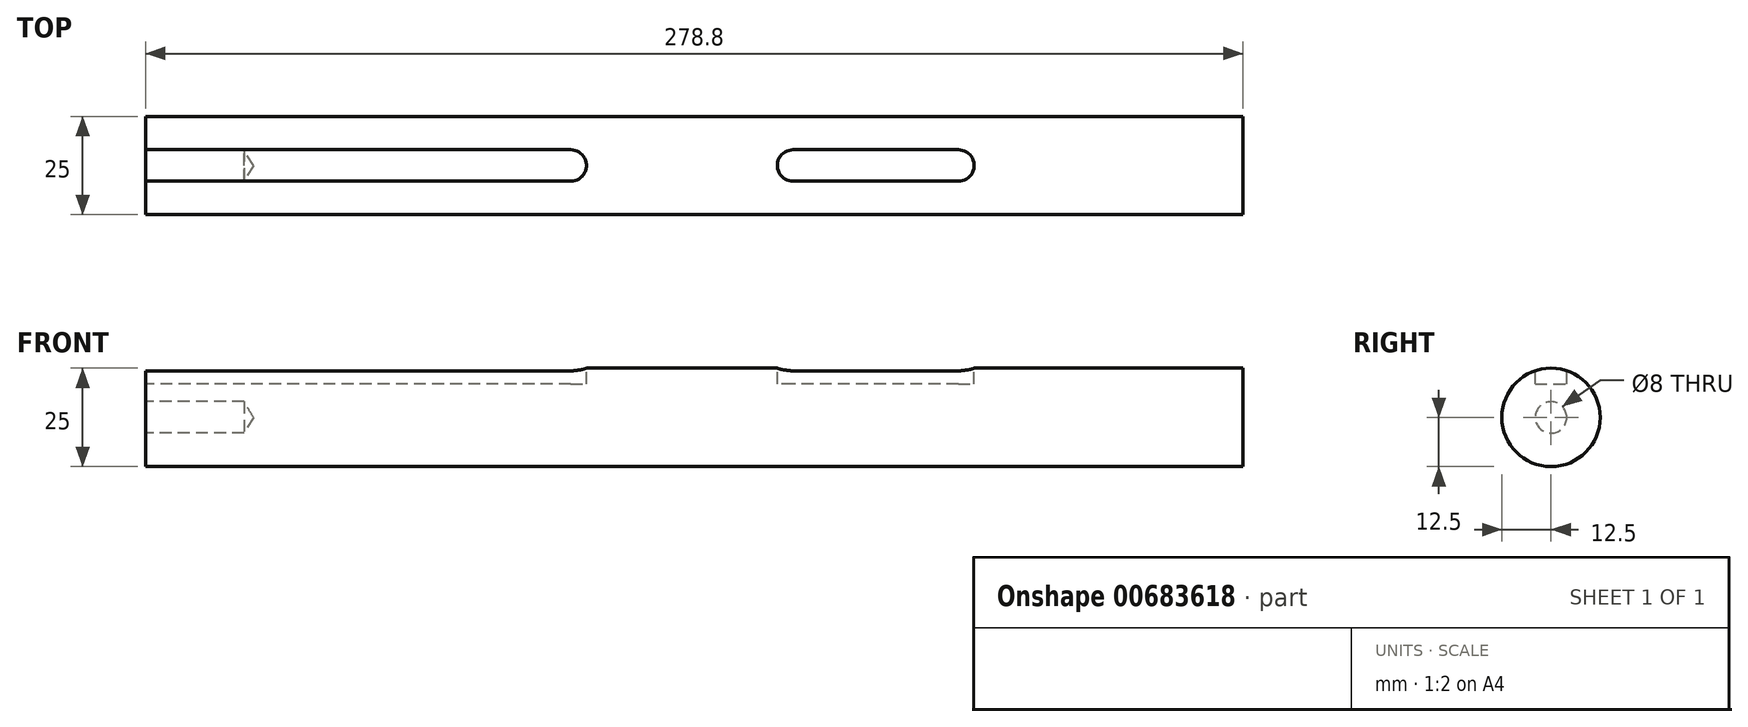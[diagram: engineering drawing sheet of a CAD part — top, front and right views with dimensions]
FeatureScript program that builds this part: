
annotation { "Feature Type Name" : "Feature", "Feature Type Description" : "" }
export const myFeature = defineFeature(function(context is Context, id is Id, definition is map)
    precondition{}
    {
        {
            var Q0;
            Q0=qCreatedBy(makeId("Front.planeOp"),FACE);
            var sketch = newSketch(context, id + "F0", { "sketchPlane" : qUnion([Q0])});
            skLineSegment(sketch, "E0", {"start": v(0, 0) * mm, "end": v(0, 12.5) * mm});
            skLineSegment(sketch, "E1", {"start": v(0, 12.5) * mm, "end": v(278.8, 12.5) * mm});
            skLineSegment(sketch, "E2", {"start": v(278.8, 12.5) * mm, "end": v(278.8, 0) * mm});
            skLineSegment(sketch, "E3", {"start": v(278.8, 0) * mm, "end": v(0, 0) * mm});
            skSolve(sketch);
        }
        {
            var Q0;
            Q0 = qSketchRegion(id + "F0", true);
            var Q1;
            Q1=sQuery(id+"F0.wireOp",EDGE,"E3");
            revolve(context, id + "F1", {"entities" : qUnion([Q0]), "axis" : qUnion([Q1]), "revolveType" : RevolveType.FULL});
        }
        {
            var Q0;
            Q0=qCreatedBy(makeId("Top.planeOp"),FACE);
            cPlane(context, id + "F2", {"entities" : qUnion([Q0]), "cplaneType" : CPlaneType.OFFSET, "offset" : 12.5 * mm, "width" : 150 * mm, "height" : 150 * mm});
        }
        {
            var Q0;
            Q0=qCreatedBy(id+"F2.planeOp",FACE);
            var sketch = newSketch(context, id + "F3", { "sketchPlane" : qUnion([Q0])});
            skLineSegment(sketch, "E4", {"start": v(0, 0) * mm, "end": v(0, 4) * mm});
            skLineSegment(sketch, "E5", {"start": v(0, 4) * mm, "end": v(108, 4) * mm});
            skLineSegment(sketch, "E6", {"start": v(112, 0) * mm, "end": v(112, 0) * mm});
            skLineSegment(sketch, "E7", {"start": v(108, -4) * mm, "end": v(0, -4) * mm});
            skLineSegment(sketch, "E8", {"start": v(0, -4) * mm, "end": v(0, 0) * mm});
            skPoint(sketch, "E9.visualSharp", {"position": v(112, 4) * mm});
            skArc(sketch, "E9.filletArc", {"start": v(112, 0) * mm, "mid": v(110.83, 2.83) * mm, "end": v(108, 4) * mm});
            skPoint(sketch, "E10.visualSharp", {"position": v(112, -4) * mm});
            skArc(sketch, "E10.filletArc", {"start": v(108, -4) * mm, "mid": v(110.83, -2.83) * mm, "end": v(112, 0) * mm});
            skSolve(sketch);
        }
        {
            var Q0;
            Q0 = qSketchRegion(id + "F3", true);
            extrude(context, id + "F4", {"entities" : qUnion([Q0]), "operationType" : NewBodyOperationType.REMOVE, "oppositeDirection" : true, "depth" : 4 * mm, "offsetDistance" : 25 * mm});
        }
        {
            var Q0;
            Q0=makeQuery(id+"F1.opRevolve","SWEPT_FACE",FACE,{"disambiguationData":[OSD([sQuery(id+"F0.wireOp",EDGE,"E0")])]});
            var sketch = newSketch(context, id + "F5", { "sketchPlane" : qUnion([Q0])});
            skCircle(sketch, "E11", {"center": v(0, 0) * mm, "radius": 4 * mm});
            skSolve(sketch);
        }
        {
            var Q0;
            Q0=sQuery(id+"F5.wireOp",VERTEX,"E11.center");
            var Q1;
            Q1=makeQuery(id+"F1.opRevolve","SWEPT_BODY",BODY,{"disambiguationData":[OSD([sQuery(id+"F0.wireOp",EDGE,"E0"),sQuery(id+"F0.wireOp",EDGE,"E1"),sQuery(id+"F0.wireOp",EDGE,"E2"),sQuery(id+"F0.wireOp",EDGE,"E3")])]});
            hole(context, id + "F6", {"style" : HoleStyle.SIMPLE, "endStyle" : HoleEndStyle.BLIND, "holeDiameter" : 8 * mm, "majorDiameter" : 5 * mm, "holeDepth" : 25 * mm, "isTappedThrough" : true, "tappedDepth" : 12 * mm, "tapClearance" : 3, "startFromSketch" : true, "locations" : qUnion([Q0]), "scope" : qUnion([Q1])});
        }
        {
            var Q0;
            Q0=qCreatedBy(id+"F2.planeOp",FACE);
            var sketch = newSketch(context, id + "F7", { "sketchPlane" : qUnion([Q0])});
            skLineSegment(sketch, "E12", {"start": v(210.5, 0) * mm, "end": v(210.5, 0) * mm});
            skLineSegment(sketch, "E13", {"start": v(206.5, 4) * mm, "end": v(164.5, 4) * mm});
            skLineSegment(sketch, "E14", {"start": v(160.5, 0) * mm, "end": v(160.5, 0) * mm});
            skLineSegment(sketch, "E15", {"start": v(164.5, -4) * mm, "end": v(206.5, -4) * mm});
            skPoint(sketch, "E16.visualSharp", {"position": v(210.5, 4) * mm});
            skArc(sketch, "E16.filletArc", {"start": v(210.5, 0) * mm, "mid": v(209.33, 2.83) * mm, "end": v(206.5, 4) * mm});
            skPoint(sketch, "E17.visualSharp", {"position": v(210.5, -4) * mm});
            skArc(sketch, "E17.filletArc", {"start": v(206.5, -4) * mm, "mid": v(209.33, -2.83) * mm, "end": v(210.5, 0) * mm});
            skPoint(sketch, "E18.visualSharp", {"position": v(160.5, 4) * mm});
            skArc(sketch, "E18.filletArc", {"start": v(164.5, 4) * mm, "mid": v(161.67, 2.83) * mm, "end": v(160.5, 0) * mm});
            skPoint(sketch, "E19.visualSharp", {"position": v(160.5, -4) * mm});
            skArc(sketch, "E19.filletArc", {"start": v(160.5, 0) * mm, "mid": v(161.67, -2.83) * mm, "end": v(164.5, -4) * mm});
            skLineSegment(sketch, "E20", {"start": v(160.5, 0) * mm, "end": v(210.5, 0) * mm, "construction": true});
            skLineSegment(sketch, "E21", {"start": v(185.5, 0) * mm, "end": v(185.5, 16.48) * mm, "construction": true});
            skLineSegment(sketch, "E22.0", {"start": v(233, 0) * mm, "end": v(233, 16.48) * mm});
            skLineSegment(sketch, "E23.0", {"start": v(138, 0) * mm, "end": v(138, 16.48) * mm});
            skSolve(sketch);
        }
        {
            var Q0;
            Q0=makeQuery(id+"F7.imprint","IMPRINT",FACE,{"disambiguationData":[TD([[makeQuery(id+"F7.imprint","IMPRINT",EDGE,{"derivedFrom":sQuery(id+"F7.wireOp",EDGE,"E13")}),1.0]])]});
            extrude(context, id + "F8", {"entities" : qUnion([Q0]), "operationType" : NewBodyOperationType.REMOVE, "oppositeDirection" : true, "depth" : 4 * mm, "offsetDistance" : 25 * mm});
        }
    });
